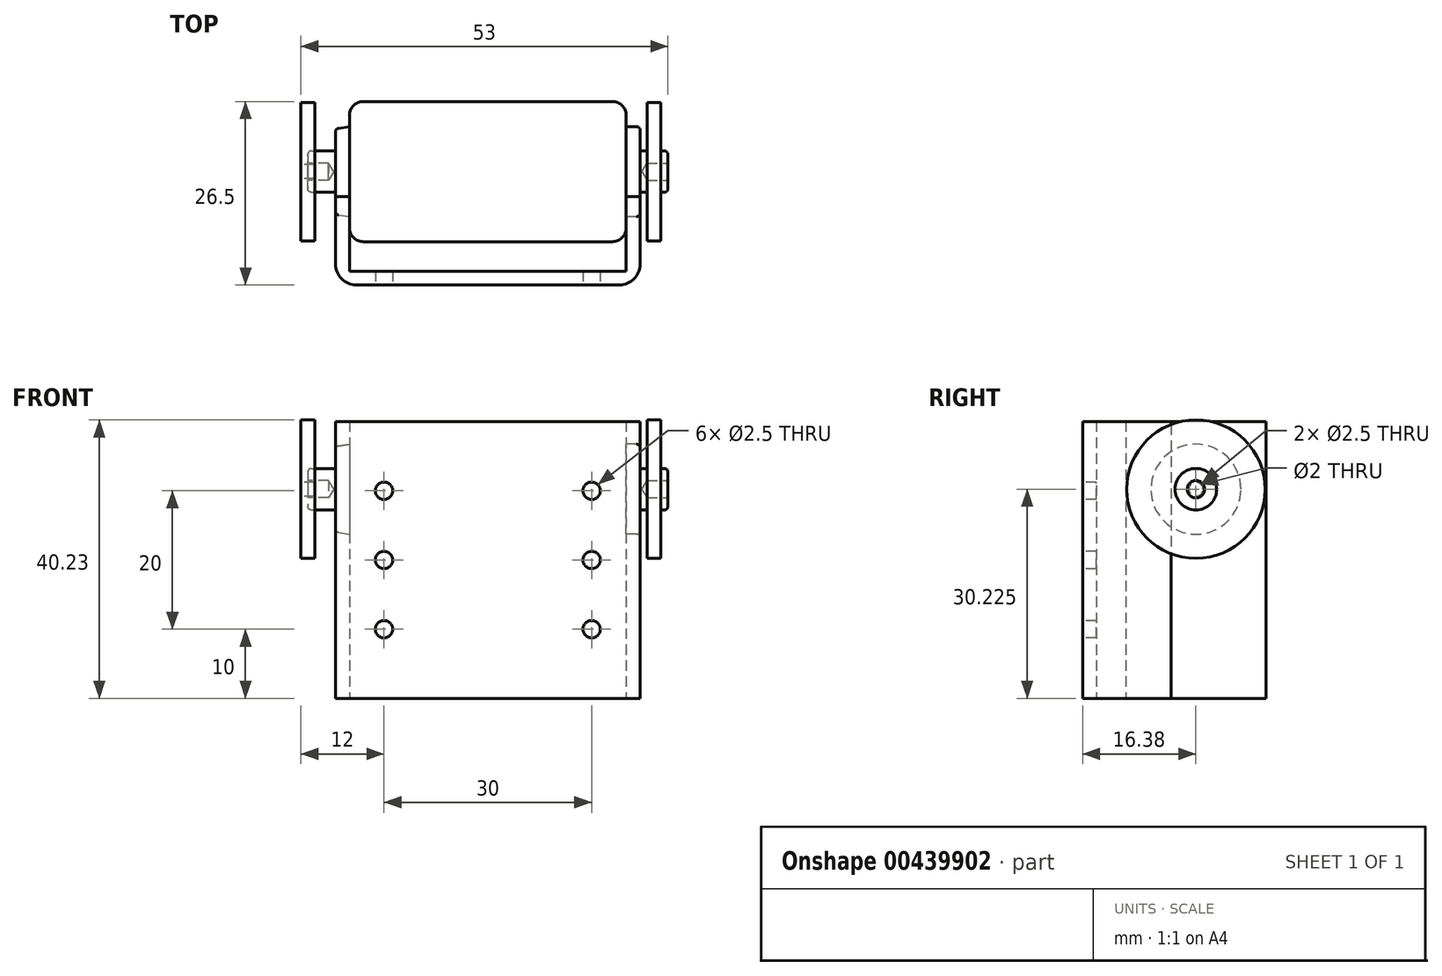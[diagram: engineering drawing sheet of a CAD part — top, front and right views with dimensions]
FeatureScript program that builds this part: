
annotation { "Feature Type Name" : "Feature", "Feature Type Description" : "" }
export const myFeature = defineFeature(function(context is Context, id is Id, definition is map)
    precondition{}
    {
        {
            var Q0;
            Q0=qCreatedBy(makeId("Top.planeOp"),FACE);
            var sketch = newSketch(context, id + "F0", { "sketchPlane" : qUnion([Q0])});
            skLineSegment(sketch, "E0.bottom", {"start": v(-20, 10.12) * mm, "end": v(20, 10.12) * mm});
            skLineSegment(sketch, "E0.top", {"start": v(-20, -10.12) * mm, "end": v(20, -10.12) * mm});
            skLineSegment(sketch, "E0.left", {"start": v(-20, 10.12) * mm, "end": v(-20, -10.12) * mm});
            skLineSegment(sketch, "E0.right", {"start": v(20, 10.12) * mm, "end": v(20, -10.12) * mm});
            skLineSegment(sketch, "E1", {"start": v(20, 10.13) * mm, "end": v(-20, -10.13) * mm, "construction": true});
            skSolve(sketch);
        }
        {
            var Q0;
            Q0=makeQuery(id+"F0.imprint","IMPRINT",FACE,{"disambiguationData":[TD([[makeQuery(id+"F0.imprint","IMPRINT",EDGE,{"derivedFrom":sQuery(id+"F0.wireOp",EDGE,"E0.bottom")}),-1.0]])]});
            extrude(context, id + "F1", {"entities" : qUnion([Q0]), "depth" : 40 * mm});
        }
        {
            var Q0;
            Q0=makeQuery(id+"F1.opExtrude","SWEPT_EDGE",EDGE,{"disambiguationData":[OSD([sQuery(id+"F0.wireOp",EDGE,"E0.bottom"),sQuery(id+"F0.wireOp",EDGE,"E0.left")])]});
            var Q1;
            Q1=makeQuery(id+"F1.opExtrude","SWEPT_EDGE",EDGE,{"disambiguationData":[OSD([sQuery(id+"F0.wireOp",EDGE,"E0.top"),sQuery(id+"F0.wireOp",EDGE,"E0.left")])]});
            var Q2;
            Q2=makeQuery(id+"F1.opExtrude","SWEPT_EDGE",EDGE,{"disambiguationData":[OSD([sQuery(id+"F0.wireOp",EDGE,"E0.bottom"),sQuery(id+"F0.wireOp",EDGE,"E0.right")])]});
            var Q3;
            Q3=makeQuery(id+"F1.opExtrude","SWEPT_EDGE",EDGE,{"disambiguationData":[OSD([sQuery(id+"F0.wireOp",EDGE,"E0.top"),sQuery(id+"F0.wireOp",EDGE,"E0.right")])]});
            fillet(context, id + "F2", {"entities" : qUnion([Q0, Q1, Q2, Q3]), "radius" : 2 * mm, "tangentPropagation" : true, "allowEdgeOverflow" : false});
        }
        {
            var Q0;
            Q0=makeQuery(id+"F1.opExtrude","SWEPT_FACE",FACE,{"disambiguationData":[OSD([sQuery(id+"F0.wireOp",EDGE,"E0.left")])]});
            var sketch = newSketch(context, id + "F3", { "sketchPlane" : qUnion([Q0])});
            skCircle(sketch, "E2", {"center": v(0, 30.23) * mm, "radius": 6.5 * mm});
            skPoint(sketch, "E3.endSnap0", {"position": v(0, 40) * mm});
            skLineSegment(sketch, "E4", {"start": v(0, 0) * mm, "end": v(0, 30.23) * mm, "construction": true});
            skSolve(sketch);
        }
        {
            var Q0;
            Q0=makeQuery(id+"F3.imprint","IMPRINT",FACE,{"disambiguationData":[TD([[makeQuery(id+"F3.imprint","IMPRINT",EDGE,{"derivedFrom":sQuery(id+"F3.wireOp",EDGE,"E2")}),1.0]])]});
            var Q1;
            Q1=sQuery(id+"F3.wireOp",EDGE,"E2");
            extrude(context, id + "F4", {"entities" : qUnion([Q0]), "operationType" : NewBodyOperationType.ADD, "surfaceEntities" : qUnion([Q1]), "depth" : 2 * mm});
        }
        {
            var Q0;
            Q0=makeQuery(id+"F4.opExtrude","CAP_FACE",FACE,{"disambiguationData":[OSD([sQuery(id+"F3.wireOp",EDGE,"E2")])],"isStart":false});
            chamfer(context, id + "F5", {"entities" : qUnion([Q0]), "chamferType" : ChamferType.TWO_OFFSETS, "width1" : 2 * mm, "oppositeDirection" : true, "width2" : 0.3 * mm, "tangentPropagation" : true});
        }
        {
            var Q0;
            {var subQ0=sQuery(id+"F3.wireOp",EDGE,"E2");Q0=makeQuery(id+"F5.opChamfer","BLEND_EDGE",EDGE,{"blendedFrom":[makeQuery(id+"F4.opExtrude","CAP_EDGE",EDGE,{"disambiguationData":[OSD([subQ0])],"isStart":false}),makeQuery(id+"F4.opExtrude","CAP_FACE",FACE,{"disambiguationData":[OSD([subQ0])],"isStart":false})],"blendedInto":[makeQuery(id+"F4.opExtrude","CAP_FACE",FACE,{"disambiguationData":[OSD([subQ0])],"isStart":false})]});}
            fillet(context, id + "F6", {"entities" : qUnion([Q0]), "radius" : 0.5 * mm, "tangentPropagation" : true, "allowEdgeOverflow" : false});
        }
        {
            var Q0;
            Q0=makeQuery(id+"F4.opExtrude","CAP_FACE",FACE,{"disambiguationData":[OSD([sQuery(id+"F3.wireOp",EDGE,"E2")])],"isStart":false});
            var sketch = newSketch(context, id + "F7", { "sketchPlane" : qUnion([Q0])});
            skCircle(sketch, "E5", {"center": v(0, 30.23) * mm, "radius": 3 * mm});
            skSolve(sketch);
        }
        {
            var Q0;
            Q0 = qSketchRegion(id + "F7", true);
            extrude(context, id + "F8", {"entities" : qUnion([Q0]), "operationType" : NewBodyOperationType.ADD, "depth" : 4 * mm});
        }
        {
            var Q0;
            Q0=makeQuery(id+"F8.opExtrude","CAP_EDGE",EDGE,{"disambiguationData":[OSD([sQuery(id+"F7.wireOp",EDGE,"E5")])],"isStart":false});
            fillet(context, id + "F9", {"entities" : qUnion([Q0]), "radius" : 0.5 * mm, "tangentPropagation" : true, "allowEdgeOverflow" : false});
        }
        {
            var Q0;
            Q0=makeQuery(id+"F1.opExtrude","SWEPT_FACE",FACE,{"disambiguationData":[OSD([sQuery(id+"F0.wireOp",EDGE,"E0.right")])]});
            var sketch = newSketch(context, id + "F10", { "sketchPlane" : qUnion([Q0])});
            skPoint(sketch, "E6.endSnap0", {"position": v(0, 40) * mm});
            skCircle(sketch, "E7", {"center": v(0, 30.23) * mm, "radius": 6.5 * mm});
            skLineSegment(sketch, "E8", {"start": v(0, 0) * mm, "end": v(0, 30.23) * mm, "construction": true});
            skSolve(sketch);
        }
        {
            var Q0;
            Q0 = qSketchRegion(id + "F10", true);
            extrude(context, id + "F11", {"entities" : qUnion([Q0]), "operationType" : NewBodyOperationType.ADD, "depth" : 2 * mm});
        }
        {
            var Q0;
            Q0=makeQuery(id+"F11.opExtrude","CAP_EDGE",EDGE,{"disambiguationData":[OSD([sQuery(id+"F10.wireOp",EDGE,"E7")])],"isStart":false});
            fillet(context, id + "F12", {"entities" : qUnion([Q0]), "radius" : 0.5 * mm, "tangentPropagation" : true, "allowEdgeOverflow" : false});
        }
        {
            var Q0;
            Q0=makeQuery(id+"F11.opExtrude","CAP_FACE",FACE,{"disambiguationData":[OSD([sQuery(id+"F10.wireOp",EDGE,"E7")])],"isStart":false});
            var sketch = newSketch(context, id + "F13", { "sketchPlane" : qUnion([Q0])});
            skCircle(sketch, "E9", {"center": v(0, 30.23) * mm, "radius": 3 * mm});
            skSolve(sketch);
        }
        {
            var Q0;
            Q0 = qSketchRegion(id + "F13", true);
            extrude(context, id + "F14", {"entities" : qUnion([Q0]), "operationType" : NewBodyOperationType.ADD, "depth" : 4 * mm});
        }
        {
            var Q0;
            Q0=makeQuery(id+"F14.opExtrude","CAP_EDGE",EDGE,{"disambiguationData":[OSD([sQuery(id+"F13.wireOp",EDGE,"E9")])],"isStart":false});
            fillet(context, id + "F15", {"entities" : qUnion([Q0]), "radius" : 0.5 * mm, "tangentPropagation" : true, "allowEdgeOverflow" : false});
        }
        {
            var Q0;
            Q0=makeQuery(id+"F8.opExtrude","CAP_FACE",FACE,{"disambiguationData":[OSD([sQuery(id+"F7.wireOp",EDGE,"E5")])],"isStart":false});
            var sketch = newSketch(context, id + "F16", { "sketchPlane" : qUnion([Q0])});
            skCircle(sketch, "E10", {"center": v(0, 30.23) * mm, "radius": 1.02 * mm, "construction": true});
            skSolve(sketch);
        }
        {
            var Q0;
            Q0=sQuery(id+"F16.wireOp",VERTEX,"E10.center");
            var Q1;
            Q1=makeQuery(id+"F1.opExtrude","SWEPT_BODY",BODY,{"disambiguationData":[OSD([sQuery(id+"F0.wireOp",EDGE,"E0.bottom"),sQuery(id+"F0.wireOp",EDGE,"E0.top"),sQuery(id+"F0.wireOp",EDGE,"E0.left"),sQuery(id+"F0.wireOp",EDGE,"E0.right")])]});
            hole(context, id + "F17", {"style" : HoleStyle.C_BORE, "endStyle" : HoleEndStyle.BLIND, "holeDiameter" : 2.5 * mm, "cBoreDiameter" : 2.5 * mm, "cBoreDepth" : 0 * mm, "holeDepth" : 3 * mm, "isTappedThrough" : true, "tappedDepth" : 12 * mm, "tapClearance" : 3, "startFromSketch" : true, "locations" : qUnion([Q0]), "scope" : qUnion([Q1])});
        }
        {
            var Q0;
            Q0=makeQuery(id+"F14.opExtrude","CAP_FACE",FACE,{"disambiguationData":[OSD([sQuery(id+"F13.wireOp",EDGE,"E9")])],"isStart":false});
            var sketch = newSketch(context, id + "F18", { "sketchPlane" : qUnion([Q0])});
            skCircle(sketch, "E11", {"center": v(0, 30.23) * mm, "radius": 0.97 * mm, "construction": true});
            skSolve(sketch);
        }
        {
            var Q0;
            Q0=sQuery(id+"F18.wireOp",VERTEX,"E11.center");
            var Q1;
            Q1=makeQuery(id+"F1.opExtrude","SWEPT_BODY",BODY,{"disambiguationData":[OSD([sQuery(id+"F0.wireOp",EDGE,"E0.bottom"),sQuery(id+"F0.wireOp",EDGE,"E0.top"),sQuery(id+"F0.wireOp",EDGE,"E0.left"),sQuery(id+"F0.wireOp",EDGE,"E0.right")])]});
            hole(context, id + "F19", {"style" : HoleStyle.C_BORE, "endStyle" : HoleEndStyle.BLIND, "holeDiameter" : 2.5 * mm, "cBoreDiameter" : 2.5 * mm, "cBoreDepth" : 0 * mm, "holeDepth" : 3 * mm, "isTappedThrough" : true, "tappedDepth" : 12 * mm, "tapClearance" : 3, "startFromSketch" : true, "locations" : qUnion([Q0]), "scope" : qUnion([Q1])});
        }
        {
            var Q0;
            Q0=makeQuery(id+"F1.opExtrude","SWEPT_FACE",FACE,{"disambiguationData":[OSD([sQuery(id+"F0.wireOp",EDGE,"E0.left")])]});
            cPlane(context, id + "F20", {"entities" : qUnion([Q0]), "cplaneType" : CPlaneType.OFFSET, "offset" : 7 * mm, "width" : 150 * mm, "height" : 150 * mm});
        }
        {
            var Q0;
            Q0=qCreatedBy(id+"F20.planeOp",FACE);
            var sketch = newSketch(context, id + "F21", { "sketchPlane" : qUnion([Q0])});
            skCircle(sketch, "E12", {"center": v(0, 30.23) * mm, "radius": 10 * mm});
            skCircle(sketch, "E13", {"center": v(0, 30.23) * mm, "radius": 1 * mm});
            skLineSegment(sketch, "E14", {"start": v(0, 0) * mm, "end": v(0, 30.23) * mm, "construction": true});
            skSolve(sketch);
        }
        {
            var Q0;
            Q0 = qSketchRegion(id + "F21", true);
            extrude(context, id + "F22", {"entities" : qUnion([Q0]), "oppositeDirection" : true, "depth" : 2 * mm});
        }
        {
            var Q0;
            Q0=makeQuery(id+"F1.opExtrude","SWEPT_FACE",FACE,{"disambiguationData":[OSD([sQuery(id+"F0.wireOp",EDGE,"E0.right")])]});
            cPlane(context, id + "F23", {"entities" : qUnion([Q0]), "cplaneType" : CPlaneType.OFFSET, "offset" : 5 * mm, "width" : 150 * mm, "height" : 150 * mm});
        }
        {
            var Q0;
            Q0=qCreatedBy(id+"F23.planeOp",FACE);
            var sketch = newSketch(context, id + "F24", { "sketchPlane" : qUnion([Q0])});
            skLineSegment(sketch, "E15", {"start": v(0, 0) * mm, "end": v(0, 30.23) * mm, "construction": true});
            skCircle(sketch, "E16", {"center": v(0, 30.23) * mm, "radius": 10 * mm});
            skCircle(sketch, "E17", {"center": v(0, 30.23) * mm, "radius": 3 * mm});
            skSolve(sketch);
        }
        {
            var Q0;
            Q0 = qSketchRegion(id + "F24", true);
            extrude(context, id + "F25", {"entities" : qUnion([Q0]), "operationType" : NewBodyOperationType.ADD, "oppositeDirection" : true, "depth" : 2 * mm});
        }
        {
            var Q0;
            Q0=qCreatedBy(makeId("Top.planeOp"),FACE);
            var sketch = newSketch(context, id + "F26", { "sketchPlane" : qUnion([Q0])});
            skLineSegment(sketch, "E18.top", {"start": v(22, -3.59) * mm, "end": v(20, -3.59) * mm});
            skLineSegment(sketch, "E18.left", {"start": v(20, -14.38) * mm, "end": v(20, -3.59) * mm});
            skLineSegment(sketch, "E18.right", {"start": v(-20, -14.38) * mm, "end": v(-20, -3.59) * mm});
            skLineSegment(sketch, "E19", {"start": v(22, -16.38) * mm, "end": v(22, -3.59) * mm});
            skLineSegment(sketch, "E20", {"start": v(-22, -16.38) * mm, "end": v(-22, -3.59) * mm});
            skLineSegment(sketch, "E21", {"start": v(22, -16.38) * mm, "end": v(-22, -16.38) * mm});
            skLineSegment(sketch, "E22.trimOffspring", {"start": v(-20, -3.59) * mm, "end": v(-22, -3.59) * mm});
            skLineSegment(sketch, "E23", {"start": v(20, -14.38) * mm, "end": v(-20, -14.38) * mm});
            skLineSegment(sketch, "E24", {"start": v(0, -16.38) * mm, "end": v(0, 10.12) * mm, "construction": true});
            skSolve(sketch);
        }
        {
            var Q0;
            Q0 = qSketchRegion(id + "F26", true);
            extrude(context, id + "F27", {"entities" : qUnion([Q0]), "depth" : 40 * mm});
        }
        {
            var Q0;
            Q0=makeQuery(id+"F27.opExtrude","SWEPT_EDGE",EDGE,{"disambiguationData":[OSD([sQuery(id+"F26.wireOp",EDGE,"E19"),sQuery(id+"F26.wireOp",EDGE,"E21")])]});
            var Q1;
            Q1=makeQuery(id+"F27.opExtrude","SWEPT_EDGE",EDGE,{"disambiguationData":[OSD([sQuery(id+"F26.wireOp",EDGE,"E20"),sQuery(id+"F26.wireOp",EDGE,"E21")])]});
            fillet(context, id + "F28", {"entities" : qUnion([Q0, Q1]), "radius" : 3 * mm, "tangentPropagation" : true, "allowEdgeOverflow" : false});
        }
        {
            var Q0;
            Q0=makeQuery(id+"F27.opExtrude","SWEPT_FACE",FACE,{"disambiguationData":[OSD([sQuery(id+"F26.wireOp",EDGE,"E21")])]});
            var sketch = newSketch(context, id + "F29", { "sketchPlane" : qUnion([Q0])});
            skCircle(sketch, "E25", {"center": v(-15, 30) * mm, "radius": 1.25 * mm, "construction": true});
            skCircle(sketch, "E26.0.1.0", {"center": v(-15, 20) * mm, "radius": 1.25 * mm, "construction": true});
            skCircle(sketch, "E26.0.2.0", {"center": v(-15, 10) * mm, "radius": 1.25 * mm, "construction": true});
            skCircle(sketch, "E26.1.0.0", {"center": v(15, 30) * mm, "radius": 1.25 * mm, "construction": true});
            skCircle(sketch, "E26.1.1.0", {"center": v(15, 20) * mm, "radius": 1.25 * mm, "construction": true});
            skCircle(sketch, "E26.1.2.0", {"center": v(15, 10) * mm, "radius": 1.25 * mm, "construction": true});
            skSolve(sketch);
        }
        {
            var Q0;
            Q0=sQuery(id+"F29.wireOp",VERTEX,"E25.center");
            var Q1;
            Q1=sQuery(id+"F29.wireOp",VERTEX,"E26.1.0.0.center");
            var Q2;
            Q2=sQuery(id+"F29.wireOp",VERTEX,"E26.1.1.0.center");
            var Q3;
            Q3=sQuery(id+"F29.wireOp",VERTEX,"E26.0.1.0.center");
            var Q4;
            Q4=sQuery(id+"F29.wireOp",VERTEX,"E26.0.2.0.center");
            var Q5;
            Q5=sQuery(id+"F29.wireOp",VERTEX,"E26.1.2.0.center");
            var Q6;
            Q6=makeQuery(id+"F27.opExtrude","SWEPT_BODY",BODY,{"disambiguationData":[OSD([sQuery(id+"F26.wireOp",EDGE,"E18.top"),sQuery(id+"F26.wireOp",EDGE,"E18.left"),sQuery(id+"F26.wireOp",EDGE,"E18.right"),sQuery(id+"F26.wireOp",EDGE,"E19"),sQuery(id+"F26.wireOp",EDGE,"E20"),sQuery(id+"F26.wireOp",EDGE,"E21"),sQuery(id+"F26.wireOp",EDGE,"E22.trimOffspring"),sQuery(id+"F26.wireOp",EDGE,"E23")])]});
            hole(context, id + "F30", {"style" : HoleStyle.SIMPLE, "endStyle" : HoleEndStyle.BLIND, "holeDiameter" : 2.5 * mm, "holeDepth" : 3 * mm, "isTappedThrough" : true, "tappedDepth" : 12 * mm, "tapClearance" : 3, "startFromSketch" : true, "locations" : qUnion([Q0, Q1, Q2, Q3, Q4, Q5]), "scope" : qUnion([Q6])});
        }
    });
